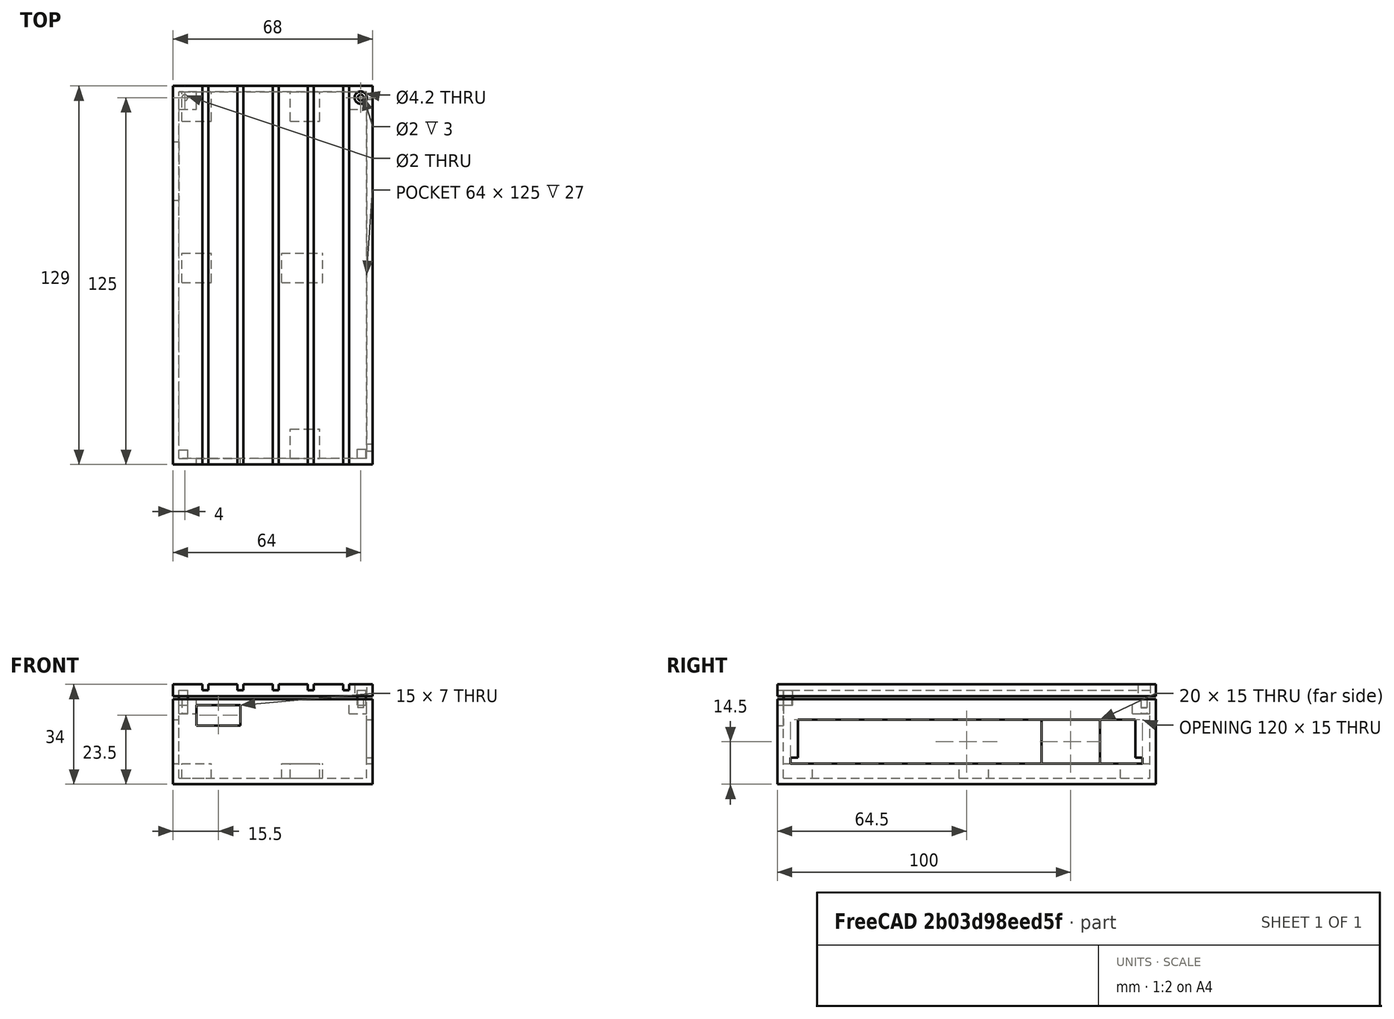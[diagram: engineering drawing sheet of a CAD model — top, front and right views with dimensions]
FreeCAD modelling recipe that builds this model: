
FCSTD DOCUMENT  (FreeCAD 0.20R29603 (Git))
Label: box1
License: All rights reserved
LicenseURL: http://en.wikipedia.org/wiki/All_rights_reserved
objects: Part::Box×22, Part::Cut×9, Part::Cylinder×4, App::DocumentObjectGroup×2, Part::MultiFuse×1
note: 36 computed .brp shape members not serialized (recipe doc carries the construction recipe); baked Part::Feature solids carry a one-line shape summary decoded from their .brp

FEATURE [Part::Box] Box  label="Cube"
  AttacherType = Attacher::AttachEngine3D
  Height = 31
  Length = 64
  Width = 125
FEATURE [Part::Box] Box001  label="Cube001"
  AttacherType = Attacher::AttachEngine3D
  Height = 29
  Length = 68
  Placement = pos=(-2,-2,-2) rot=(0,0,1;0rad)
  Width = 129
FEATURE [Part::Cut] Cut
  Base = -> Box001
  Tool = -> Box
FEATURE [Part::Box] Box002  label="netsock"
  AttacherType = Attacher::AttachEngine3D
  Height = 15
  Length = 78
  Placement = pos=(31,5,5) rot=(0,0,1;0rad)
  Width = 115
FEATURE [Part::Cut] Cut001
  Base = -> Cut
  Tool = -> Box002
FEATURE [Part::Box] Box003  label="switch"
  AttacherType = Attacher::AttachEngine3D
  Height = 15
  Length = 10
  Placement = pos=(-5,88,5) rot=(0,0,1;0rad)
  Width = 20
FEATURE [Part::Cut] Cut002
  Base = -> Cut001
  Tool = -> Box003
FEATURE [Part::Box] Box004  label="usb"
  AttacherType = Attacher::AttachEngine3D
  Height = 7
  Length = 15
  Placement = pos=(6,-3,18) rot=(0,0,1;0rad)
  Width = 10
FEATURE [Part::Cut] Cut003
  Base = -> Cut002
  Placement = pos=(14,0,0) rot=(0,0,1;0rad)
  Tool = -> Box004
FEATURE [Part::Box] Box005  label="Cube002"
  AttacherType = Attacher::AttachEngine3D
  Height = 5
  Length = 10
  Placement = pos=(52,0,0) rot=(0,0,1;0rad)
  Width = 10
FEATURE [Part::Box] Box006  label="Cube003"
  AttacherType = Attacher::AttachEngine3D
  Height = 5
  Length = 10
  Placement = pos=(15,115,0) rot=(0,0,1;0rad)
  Width = 10
FEATURE [Part::Box] Box007  label="Cube004"
  AttacherType = Attacher::AttachEngine3D
  Height = 5
  Length = 10
  Placement = pos=(52,115,0) rot=(0,0,1;0rad)
  Width = 10
FEATURE [Part::Box] Box008  label="Cube005"
  AttacherType = Attacher::AttachEngine3D
  Height = 5
  Length = 6
  Placement = pos=(72,119,22) rot=(0,0,1;0rad)
  Width = 6
FEATURE [Part::Box] Box009  label="Cube006"
  AttacherType = Attacher::AttachEngine3D
  Height = 5
  Length = 14
  Placement = pos=(49,60,0) rot=(0,0,1;0rad)
  Width = 10
FEATURE [Part::Box] Box010  label="Cube007"
  AttacherType = Attacher::AttachEngine3D
  Height = 5
  Length = 10
  Placement = pos=(15,60,0) rot=(0,0,1;0rad)
  Width = 10
FEATURE [Part::Box] Box011  label="Cube008"
  AttacherType = Attacher::AttachEngine3D
  Height = 5
  Length = 6
  Placement = pos=(0,119,22) rot=(0,0,1;0rad)
  Width = 6
FEATURE [Part::Box] Box012  label="Cube009"
  AttacherType = Attacher::AttachEngine3D
  Height = 2
  Length = 68
  Placement = pos=(-2,-2,28) rot=(0,0,1;0rad)
  Width = 129
FEATURE [Part::Box] Box014  label="Cube011"
  AttacherType = Attacher::AttachEngine3D
  Height = 2
  Length = 10
  Placement = pos=(-2,-2,30) rot=(0,0,1;0rad)
  Width = 129
FEATURE [Part::Box] Box015  label="Cube012"
  AttacherType = Attacher::AttachEngine3D
  Height = 2
  Length = 10
  Placement = pos=(10,-2,30) rot=(0,0,1;0rad)
  Width = 129
FEATURE [Part::Box] Box016  label="Cube013"
  AttacherType = Attacher::AttachEngine3D
  Height = 2
  Length = 10
  Placement = pos=(22,-2,30) rot=(0,0,1;0rad)
  Width = 129
FEATURE [Part::Box] Box017  label="Cube014"
  AttacherType = Attacher::AttachEngine3D
  Height = 2
  Length = 10
  Placement = pos=(34,-2,30) rot=(0,0,1;0rad)
  Width = 129
FEATURE [Part::Box] Box018  label="Cube015"
  AttacherType = Attacher::AttachEngine3D
  Height = 2
  Length = 10
  Placement = pos=(46,-2,30) rot=(0,0,1;0rad)
  Width = 129
FEATURE [Part::Cylinder] Cylinder
  Angle = 360
  AttacherType = Attacher::AttachEngine3D
  FirstAngle = 0
  Height = 10
  Placement = pos=(2,123,21) rot=(0,0,1;0rad)
  Radius = 1
  SecondAngle = 0
FEATURE [Part::Cylinder] Cylinder001
  Angle = 360
  AttacherType = Attacher::AttachEngine3D
  FirstAngle = 0
  Height = 10
  Placement = pos=(2,123,28) rot=(0,0,1;0rad)
  Radius = 2.1
  SecondAngle = 0
FEATURE [Part::Cylinder] Cylinder002
  Angle = 360
  AttacherType = Attacher::AttachEngine3D
  FirstAngle = 0
  Height = 10
  Placement = pos=(76,123,26) rot=(0,0,1;0rad)
  Radius = 2.1
  SecondAngle = 0
FEATURE [Part::Cylinder] Cylinder003
  Angle = 360
  AttacherType = Attacher::AttachEngine3D
  FirstAngle = 0
  Height = 10
  Placement = pos=(76,123,24) rot=(0,0,1;0rad)
  Radius = 1
  SecondAngle = 0
FEATURE [Part::Box] Box020  label="Cube017"
  AttacherType = Attacher::AttachEngine3D
  Height = 5
  Length = 3
  Placement = pos=(74.8,0.2,25) rot=(0,0,1;0rad)
  Width = 3
FEATURE [Part::Box] Box021  label="Cube018"
  AttacherType = Attacher::AttachEngine3D
  Height = 5
  Length = 3
  Placement = pos=(14,0,25) rot=(0,0,1;0rad)
  Width = 3
FEATURE [Part::Cut] Cut006
  Base = -> Box011
  Placement = pos=(14,0,0) rot=(0,0,1;0rad)
  Tool = -> Cylinder
FEATURE [Part::Cut] Cut007
  Base = -> Box008
  Tool = -> Cylinder003
FEATURE [Part::Box] Box022  label="Cube019"
  AttacherType = Attacher::AttachEngine3D
  Height = 2
  Length = 10
  Placement = pos=(72,2.5,5) rot=(0,0,1;0rad)
  Width = 120
FEATURE [Part::Cut] Cut008
  Base = -> Cut003
  Tool = -> Box022
FEATURE [App::DocumentObjectGroup] Group  label="Body"
  Group = -> [Box005,Box006,Box007,Box009,Box010,Cut006,Cut007,Cut008]
FEATURE [Part::Box] Box019  label="Cube016"
  AttacherType = Attacher::AttachEngine3D
  Height = 2
  Length = 8
  Placement = pos=(58,-2,30) rot=(0,0,1;0rad)
  Width = 129
FEATURE [Part::MultiFuse] Fusion
  Placement = pos=(14,0,0) rot=(0,0,1;0rad)
  Shapes = -> [Box012,Box014,Box015,Box016,Box017,Box018,Box019]
FEATURE [Part::Cut] Cut004
  Base = -> Fusion
  Tool = -> Cylinder001
FEATURE [Part::Cut] Cut005
  Base = -> Cut004
  Tool = -> Cylinder002
FEATURE [App::DocumentObjectGroup] Group001  label="Lid"
  Group = -> [Cut005,Box020,Box021]
